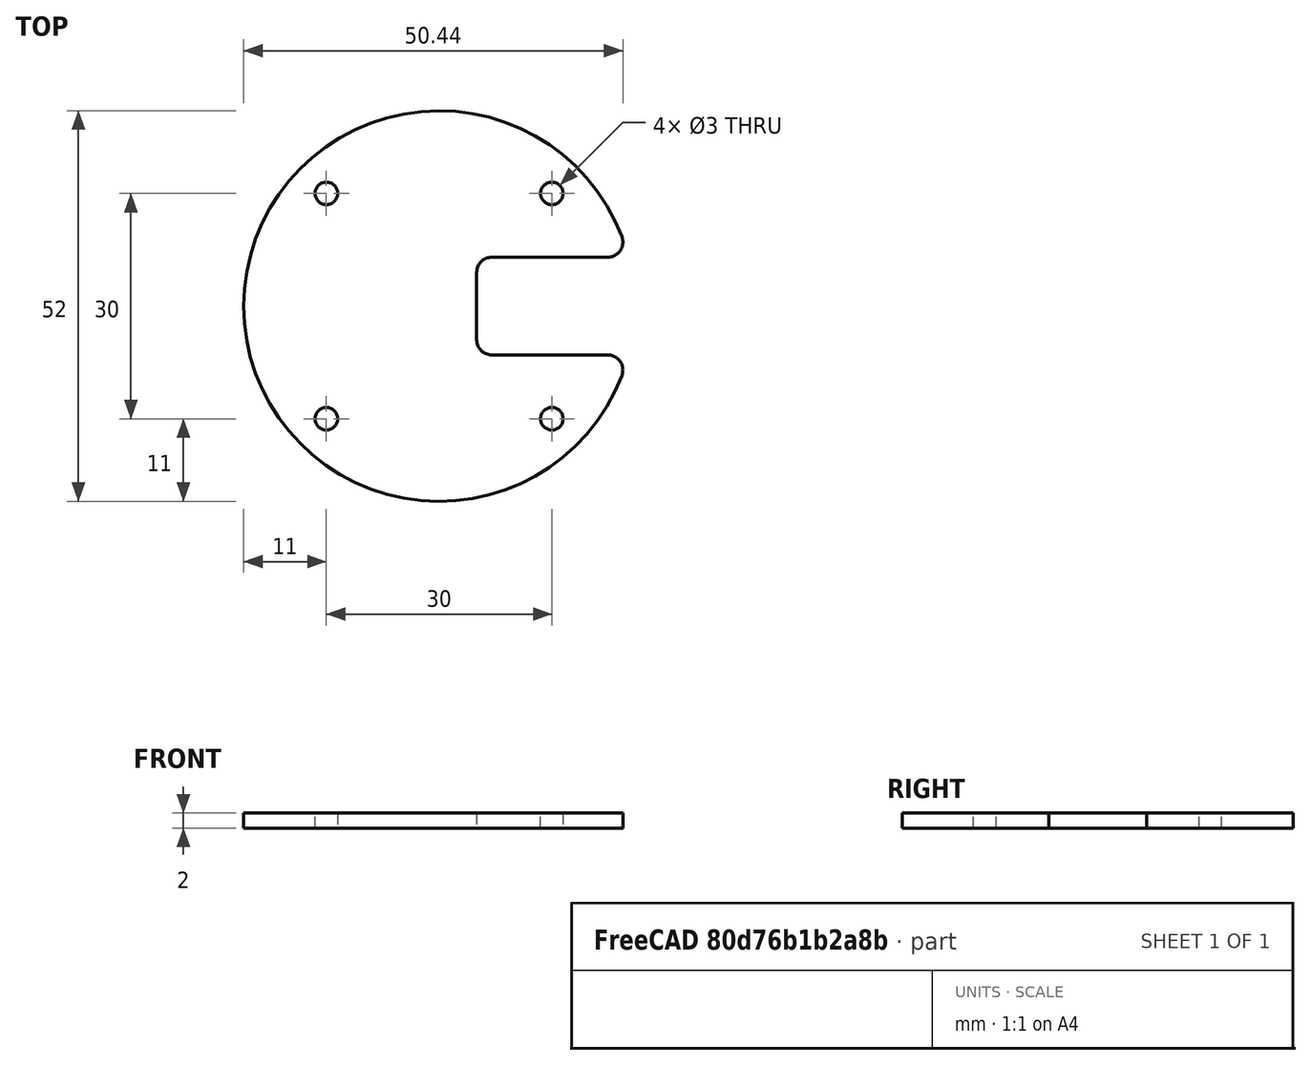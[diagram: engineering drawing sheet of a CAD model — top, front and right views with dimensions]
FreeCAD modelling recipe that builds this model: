
FCSTD DOCUMENT  (FreeCAD 0.21R33771 (Git))
Label: base_lid
License: All rights reserved
LicenseURL: http://en.wikipedia.org/wiki/All_rights_reserved
objects: Sketcher::SketchObject×3, PartDesign::Pocket×2, PartDesign::Pad×1, PartDesign::Fillet×1, PartDesign::Body×1
note: 12 computed .brp shape members not serialized (recipe doc carries the construction recipe); baked Part::Feature solids carry a one-line shape summary decoded from their .brp

FEATURE [Sketcher::SketchObject] Sketch
  FullyConstrained = false
  MapMode = 5
  Support = -> [XY_Plane]
  sketch-geometry (1):
    g0: Circle CenterX=0 CenterY=0 CenterZ=0 NormalX=0 NormalY=0 NormalZ=1 AngleXU=0 Radius=26
  constraints (1):
    c: Coincident(g0,g-1)
FEATURE [PartDesign::Pad] Pad
  Direction = (0,0,1)
  Length = 2
  Length2 = 10
  Profile = -> Sketch
  ReferenceAxis = -> Sketch [N_Axis]
  Type = 0
FEATURE [Sketcher::SketchObject] Sketch001
  FullyConstrained = false
  MapMode = 5
  Placement = pos=(0,0,2) rot=(0,0,1;0rad)
  Support = -> [Pad]
  sketch-geometry (4):
    g0: Circle CenterX=-15 CenterY=15 CenterZ=0 NormalX=0 NormalY=0 NormalZ=1 AngleXU=0 Radius=1.5
    g1: Circle CenterX=15 CenterY=15 CenterZ=0 NormalX=0 NormalY=0 NormalZ=1 AngleXU=0 Radius=1.5
    g2: Circle CenterX=15 CenterY=-15 CenterZ=0 NormalX=0 NormalY=0 NormalZ=1 AngleXU=0 Radius=1.5
    g3: Circle CenterX=-15 CenterY=-15 CenterZ=0 NormalX=0 NormalY=0 NormalZ=1 AngleXU=0 Radius=1.5
FEATURE [PartDesign::Pocket] Pocket
  BaseFeature = -> Pad
  Direction = (0,0,-1)
  Length = 5
  Length2 = 5
  Profile = -> Sketch001
  ReferenceAxis = -> Sketch001 [N_Axis]
  Type = 1
FEATURE [Sketcher::SketchObject] Sketch002
  FullyConstrained = false
  MapMode = 5
  Placement = pos=(0,0,2) rot=(0,0,1;0rad)
  Support = -> [Pocket]
  sketch-geometry (4):
    g0: LineSegment StartX=26 StartY=6.5 StartZ=0 EndX=5 EndY=6.5 EndZ=0
    g1: LineSegment StartX=5 StartY=6.5 StartZ=0 EndX=5 EndY=-6.50714 EndZ=0
    g2: LineSegment StartX=5 StartY=-6.50714 StartZ=0 EndX=26 EndY=-6.50714 EndZ=0
    g3: LineSegment StartX=26 StartY=-6.50714 StartZ=0 EndX=26 EndY=6.5 EndZ=0
  constraints (8):
    c: Coincident(g0,g1)
    c: Coincident(g1,g2)
    c: Coincident(g2,g3)
    c: Coincident(g3,g0)
    c: Horizontal(g0)
    c: Horizontal(g2)
    c: Vertical(g1)
    c: Vertical(g3)
FEATURE [PartDesign::Pocket] Pocket001
  BaseFeature = -> Pocket
  Direction = (0,0,-1)
  Length = 5
  Length2 = 5
  Profile = -> Sketch002
  ReferenceAxis = -> Sketch002 [N_Axis]
  Type = 0
FEATURE [PartDesign::Fillet] Fillet
  Base = -> Pocket001 [Edge20,Edge13,Edge2,Edge4]
  BaseFeature = -> Pocket001
  Radius = 2
  SupportTransform = false
  UseAllEdges = false
FEATURE [PartDesign::Body] Body
  Group = -> [Sketch,Pad,Sketch001,Pocket,Sketch002,Pocket001,Fillet]
  Origin = -> Origin
  Tip = -> Fillet
